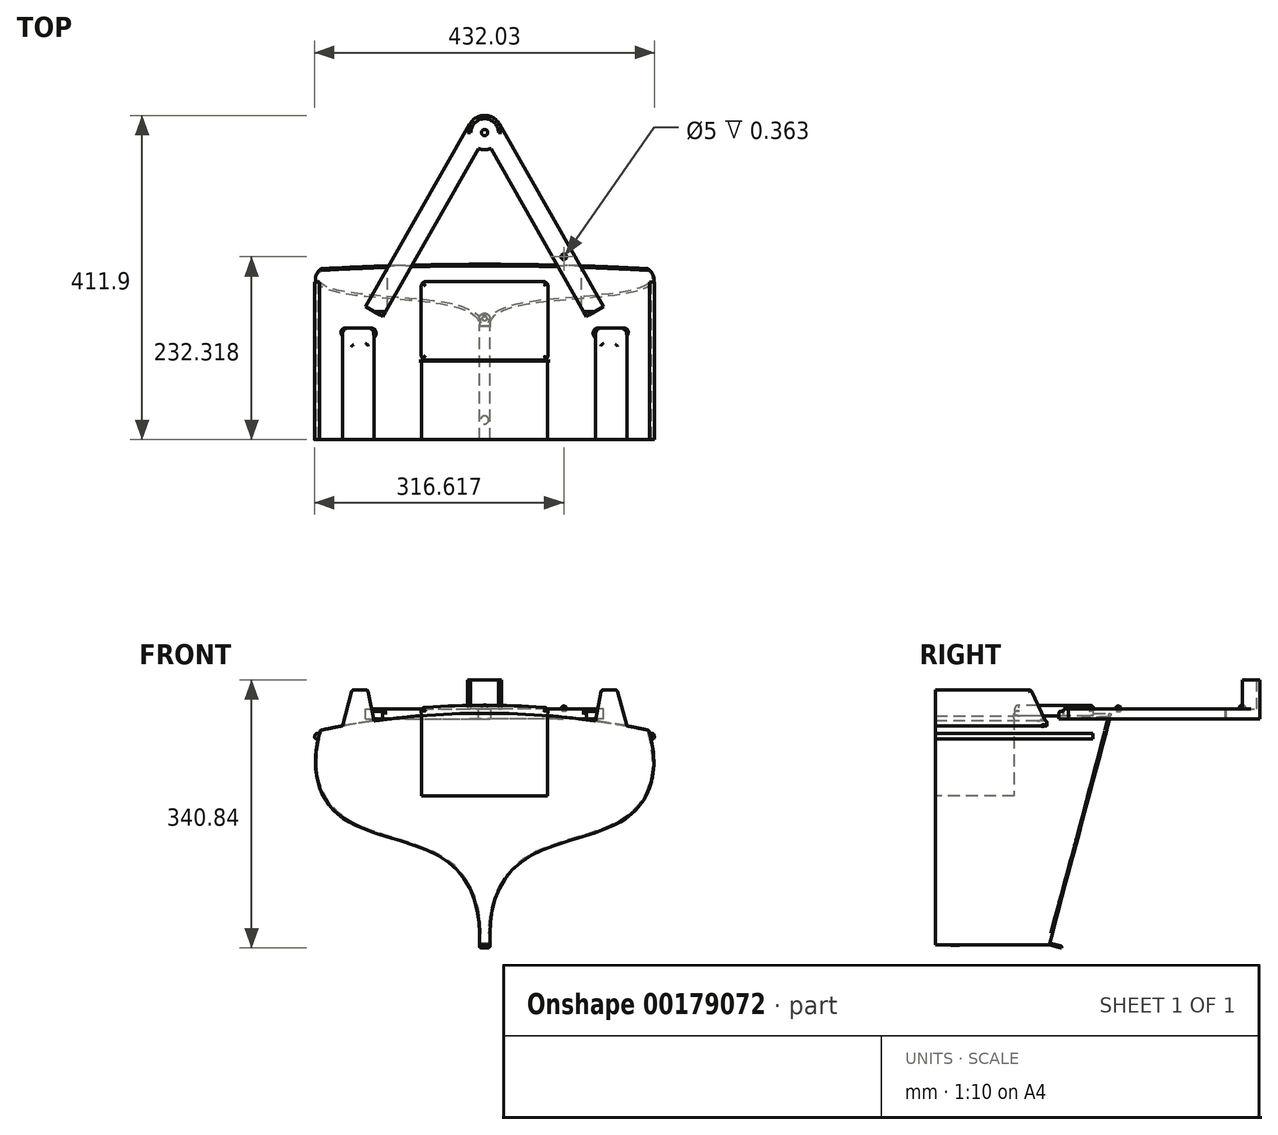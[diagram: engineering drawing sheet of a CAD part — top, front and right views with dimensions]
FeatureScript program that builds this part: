
annotation { "Feature Type Name" : "Feature", "Feature Type Description" : "" }
export const myFeature = defineFeature(function(context is Context, id is Id, definition is map)
    precondition{}
    {
        {
            var Q0;
            Q0=qCreatedBy(makeId("Front.planeOp"),FACE);
            var sketch = newSketch(context, id + "F0", { "sketchPlane" : qUnion([Q0])});
            skLineSegment(sketch, "E0", {"start": v(-1.33, 107.49) * mm, "end": v(-1.33, -186.7) * mm});
            skLineSegment(sketch, "E1", {"start": v(-1.33, -186.7) * mm, "end": v(-8, -186.7) * mm});
            skLineSegment(sketch, "E2", {"start": v(-1.33, -186.7) * mm, "end": v(-1.33, -544.52) * mm});
            skLineSegment(sketch, "E3", {"start": v(-8, -186.7) * mm, "end": v(-8, -172.3) * mm});
            skFitSpline(sketch, "E4", {"points": [v(-8, -172.3) * mm, v(-51.5, -78.76) * mm, v(-184.88, -23.02) * mm, v(-209.95, 85.87) * mm], "startDerivative": vector(0, 354.93) * mm, "endDerivative": vector(127.36, 421.05) * mm});
            skFitSpline(sketch, "E5.MirrorCS", {"points": [v(5.35, -172.3) * mm, v(48.84, -78.76) * mm, v(182.22, -23.02) * mm, v(207.3, 85.87) * mm], "startDerivative": vector(0, 354.93) * mm, "endDerivative": vector(-127.36, 421.05) * mm});
            skLineSegment(sketch, "E6.MirrorCS", {"start": v(5.35, -186.7) * mm, "end": v(5.35, -172.3) * mm});
            skLineSegment(sketch, "E7.MirrorCS", {"start": v(-1.33, -186.7) * mm, "end": v(5.35, -186.7) * mm});
            skArc(sketch, "E8", {"start": v(207.3, 85.87) * mm, "mid": v(-1.33, 107.49) * mm, "end": v(-209.95, 85.87) * mm});
            skSolve(sketch);
        }
        {
            var Q0;
            {var subQ2=sQuery(id+"F0.wireOp",EDGE,"E0");Q0=makeQuery(id+"F0.imprint","IMPRINT",FACE,{"disambiguationData":[TD([[makeQuery(id+"F0.imprint","IMPRINT",EDGE,{"derivedFrom":subQ2}),-1.0]])]});}
            var Q1;
            {var subQ1=sQuery(id+"F0.wireOp",EDGE,"E0");Q1=makeQuery(id+"F0.imprint","IMPRINT",FACE,{"disambiguationData":[TD([[makeQuery(id+"F0.imprint","IMPRINT",EDGE,{"derivedFrom":subQ1}),1.0]])]});}
            extrude(context, id + "F1", {"entities" : qUnion([Q0, Q1]), "depth" : 250 * mm});
        }
        {
            var Q0;
            Q0=qCreatedBy(makeId("Right.planeOp"),FACE);
            var sketch = newSketch(context, id + "F2", { "sketchPlane" : qUnion([Q0])});
            skLineSegment(sketch, "E9", {"start": v(-105.35, -186.7) * mm, "end": v(-3.4, 193.82) * mm});
            skLineSegment(sketch, "E10", {"start": v(-3.4, 193.82) * mm, "end": v(124.64, 193.82) * mm});
            skLineSegment(sketch, "E11", {"start": v(124.64, 193.82) * mm, "end": v(124.64, -248.32) * mm});
            skLineSegment(sketch, "E12.0", {"start": v(-250, -186.7) * mm, "end": v(0, -186.7) * mm});
            skLineSegment(sketch, "E13", {"start": v(-105.35, -186.7) * mm, "end": v(124.64, -248.32) * mm});
            skSolve(sketch);
        }
        {
            var Q0;
            Q0=makeQuery(id+"F2.imprint","IMPRINT",FACE,{"disambiguationData":[TD([[makeQuery(id+"F2.imprint","IMPRINT",EDGE,{"derivedFrom":sQuery(id+"F2.wireOp",EDGE,"E9")}),-1.0]])]});
            extrude(context, id + "F3", {"entities" : qUnion([Q0]), "operationType" : NewBodyOperationType.REMOVE, "endBound" : BoundingType.SYMMETRIC, "oppositeDirection" : true, "depth" : 500 * mm});
        }
        {
            var Q0;
            Q0=makeQuery(id+"F3.boolean.opBoolean","COPY",FACE,{"derivedFrom":makeQuery(id+"F3.opExtrude","SWEPT_FACE",FACE,{"disambiguationData":[OSD([sQuery(id+"F2.wireOp",EDGE,"E9")])]})});
            var sketch = newSketch(context, id + "F4", { "sketchPlane" : qUnion([Q0])});
            skLineSegment(sketch, "E14.bottom", {"start": v(8, -207.6) * mm, "end": v(-5.35, -207.6) * mm});
            skLineSegment(sketch, "E14.top", {"start": v(8, -205.26) * mm, "end": v(-5.35, -205.26) * mm});
            skLineSegment(sketch, "E14.left", {"start": v(8, -207.6) * mm, "end": v(8, -205.26) * mm});
            skLineSegment(sketch, "E14.right", {"start": v(-5.35, -207.6) * mm, "end": v(-5.35, -205.26) * mm});
            skSolve(sketch);
        }
        {
            var Q0;
            Q0=makeQuery(id+"F4.imprint","IMPRINT",FACE,{"disambiguationData":[TD([[makeQuery(id+"F4.imprint","IMPRINT",EDGE,{"derivedFrom":sQuery(id+"F4.wireOp",EDGE,"E14.bottom")}),-1.0]])]});
            extrude(context, id + "F5", {"entities" : qUnion([Q0]), "operationType" : NewBodyOperationType.ADD, "depth" : 16 * mm});
        }
        {
            var Q0;
            Q0=makeQuery(id+"F5.opExtrude","CAP_EDGE",EDGE,{"disambiguationData":[OSD([sQuery(id+"F4.wireOp",EDGE,"E14.right")])],"isStart":false});
            var Q1;
            Q1=makeQuery(id+"F5.opExtrude","CAP_EDGE",EDGE,{"disambiguationData":[OSD([sQuery(id+"F4.wireOp",EDGE,"E14.left")])],"isStart":false});
            fillet(context, id + "F6", {"entities" : qUnion([Q0, Q1]), "radius" : 6.6 * mm, "tangentPropagation" : true, "allowEdgeOverflow" : false});
        }
        {
            var Q0;
            Q0=makeQuery(id+"F5.opExtrude","SWEPT_FACE",FACE,{"disambiguationData":[OSD([sQuery(id+"F4.wireOp",EDGE,"E14.top")])]});
            var sketch = newSketch(context, id + "F7", { "sketchPlane" : qUnion([Q0])});
            skLineSegment(sketch, "E15", {"start": v(-1.33, -53.44) * mm, "end": v(-1.4, -44.04) * mm});
            skCircle(sketch, "E16", {"center": v(-1.4, -44.04) * mm, "radius": 3 * mm});
            skSolve(sketch);
        }
        {
            var Q0;
            Q0=makeQuery(id+"F7.imprint","IMPRINT",FACE,{"disambiguationData":[TD([[makeQuery(id+"F7.imprint","IMPRINT",EDGE,{"derivedFrom":sQuery(id+"F7.wireOp",EDGE,"E16")}),1.0]])]});
            extrude(context, id + "F8", {"entities" : qUnion([Q0]), "operationType" : NewBodyOperationType.REMOVE, "oppositeDirection" : true, "depth" : 25 * mm});
        }
        {
            var Q0;
            Q0=qCreatedBy(makeId("Top.planeOp"),FACE);
            cPlane(context, id + "F9", {"entities" : qUnion([Q0]), "cplaneType" : CPlaneType.OFFSET, "offset" : 110 * mm, "width" : 150 * mm, "height" : 150 * mm});
        }
        {
            var Q0;
            Q0=qCreatedBy(id+"F9.planeOp",FACE);
            var sketch = newSketch(context, id + "F10", { "sketchPlane" : qUnion([Q0])});
            skLineSegment(sketch, "E17.0.0", {"start": v(5.35, -104.75) * mm, "end": v(-8, -104.75) * mm});
            skLineSegment(sketch, "E17.0.1", {"start": v(-8, -104.75) * mm, "end": v(-8, -101.5) * mm});
            skFitSpline(sketch, "E17.0.2", {"points": [v(-8, -101.5) * mm, v(-8, -100.45) * mm, v(-8.3, -98.35) * mm, v(-9.41, -95.75) * mm, v(-10.8, -93.7) * mm, v(-12.1, -92.15) * mm, v(-13.69, -90.62) * mm, v(-15.53, -89.13) * mm, v(-17.67, -87.66) * mm, v(-20.1, -86.23) * mm, v(-22.84, -84.82) * mm, v(-25.92, -83.45) * mm, v(-29.28, -82.15) * mm, v(-32.93, -80.9) * mm, v(-36.88, -79.72) * mm, v(-40.43, -78.8) * mm, v(-43.42, -78.08) * mm, v(-45.74, -77.57) * mm, v(-48.1, -77.08) * mm, v(-51.32, -76.45) * mm, v(-55.43, -75.73) * mm, v(-60.5, -74.95) * mm, v(-65.68, -74.24) * mm, v(-72.72, -73.36) * mm, v(-81.71, -72.38) * mm, v(-92.72, -71.33) * mm, v(-103.87, -70.36) * mm, v(-115.1, -69.44) * mm, v(-126.32, -68.52) * mm, v(-137.49, -67.57) * mm, v(-148.54, -66.54) * mm, v(-157.59, -65.58) * mm, v(-164.69, -64.73) * mm, v(-169.92, -64.03) * mm, v(-175.06, -63.27) * mm, v(-180, -62.45) * mm, v(-184.72, -61.55) * mm, v(-188.43, -60.73) * mm, v(-191.27, -60.03) * mm, v(-193.34, -59.49) * mm, v(-195.33, -58.92) * mm, v(-197.22, -58.33) * mm, v(-199.02, -57.74) * mm, v(-201.3, -56.92) * mm, v(-203.9, -55.86) * mm, v(-206.68, -54.54) * mm, v(-209.1, -53.16) * mm, v(-211.18, -51.72) * mm, v(-212.87, -50.26) * mm, v(-214.21, -48.8) * mm, v(-215.2, -47.3) * mm, v(-215.88, -45.8) * mm, v(-216.25, -44.27) * mm, v(-216.33, -42.74) * mm, v(-216.06, -40.73) * mm, v(-215.08, -38.23) * mm, v(-213, -35.26) * mm, v(-211.05, -33.3) * mm, v(-209.95, -32.32) * mm]});
            skEllipticalArc(sketch, "E17.0.3", {});
            skFitSpline(sketch, "E17.0.4", {"points": [v(207.3, -32.32) * mm, v(208.4, -33.3) * mm, v(210.34, -35.26) * mm, v(212.42, -38.23) * mm, v(213.4, -40.73) * mm, v(213.67, -42.74) * mm, v(213.6, -44.27) * mm, v(213.23, -45.8) * mm, v(212.55, -47.3) * mm, v(211.56, -48.8) * mm, v(210.22, -50.26) * mm, v(208.53, -51.72) * mm, v(206.45, -53.16) * mm, v(204.03, -54.54) * mm, v(201.25, -55.86) * mm, v(198.64, -56.92) * mm, v(196.37, -57.74) * mm, v(194.57, -58.33) * mm, v(192.68, -58.92) * mm, v(190.68, -59.49) * mm, v(188.62, -60.03) * mm, v(185.78, -60.73) * mm, v(182.06, -61.55) * mm, v(177.35, -62.45) * mm, v(172.4, -63.27) * mm, v(167.27, -64.03) * mm, v(162.03, -64.73) * mm, v(154.93, -65.58) * mm, v(145.88, -66.54) * mm, v(134.83, -67.57) * mm, v(123.66, -68.52) * mm, v(112.44, -69.44) * mm, v(101.22, -70.36) * mm, v(90.07, -71.33) * mm, v(79.06, -72.38) * mm, v(70.07, -73.36) * mm, v(63.03, -74.24) * mm, v(57.85, -74.95) * mm, v(52.78, -75.73) * mm, v(48.67, -76.45) * mm, v(45.46, -77.08) * mm, v(43.09, -77.57) * mm, v(40.76, -78.08) * mm, v(37.77, -78.8) * mm, v(34.23, -79.72) * mm, v(30.28, -80.9) * mm, v(26.62, -82.15) * mm, v(23.27, -83.45) * mm, v(20.19, -84.82) * mm, v(17.44, -86.23) * mm, v(15.01, -87.66) * mm, v(12.88, -89.13) * mm, v(11.03, -90.62) * mm, v(9.45, -92.15) * mm, v(8.15, -93.7) * mm, v(6.76, -95.75) * mm, v(5.64, -98.35) * mm, v(5.35, -100.45) * mm, v(5.35, -101.5) * mm]});
            skLineSegment(sketch, "E17.0.5", {"start": v(5.35, -101.5) * mm, "end": v(5.35, -104.75) * mm});
            skLineSegment(sketch, "E18", {"start": v(-1.33, -26.53) * mm, "end": v(-1.33, 140.14) * mm});
            skArc(sketch, "E19", {"start": v(17.58, 150.92) * mm, "mid": v(-1.33, 161.9) * mm, "end": v(-20.24, 150.92) * mm});
            skLineSegment(sketch, "E20", {"start": v(119.81, -28.47) * mm, "end": v(17.58, 150.92) * mm});
            skLineSegment(sketch, "E21", {"start": v(119.81, -28.47) * mm, "end": v(149.75, -81) * mm});
            skLineSegment(sketch, "E22", {"start": v(149.75, -81) * mm, "end": v(128.03, -93.38) * mm});
            skLineSegment(sketch, "E23", {"start": v(128.03, -93.38) * mm, "end": v(6.52, 119.84) * mm});
            skLineSegment(sketch, "E24.MirrorCS", {"start": v(-130.68, -93.38) * mm, "end": v(-9.17, 119.84) * mm});
            skLineSegment(sketch, "E25.MirrorCS", {"start": v(-122.46, -28.47) * mm, "end": v(-20.24, 150.92) * mm});
            skLineSegment(sketch, "E26.MirrorCS", {"start": v(-122.46, -28.47) * mm, "end": v(-152.4, -81) * mm});
            skLineSegment(sketch, "E27.MirrorCS", {"start": v(-152.4, -81) * mm, "end": v(-130.68, -93.38) * mm});
            skArc(sketch, "E28.trimOffspring", {"start": v(-9.17, 119.84) * mm, "mid": v(-1.33, 118.38) * mm, "end": v(6.52, 119.84) * mm});
            const initialGuessF10  = {"E17.0.3": [-0.001326968142953605, -0.29910888352147796, 1, 0, 1.0172835059924696, 0.27258029390418276, 1.3642566717496463, 1.777335981840147]};
            skSetInitialGuess(sketch, initialGuessF10);
            skSolve(sketch);
        }
        {
            var Q0;
            Q0=makeQuery(id+"F10.imprint","IMPRINT",FACE,{"disambiguationData":[TD([[makeQuery(id+"F10.imprint","IMPRINT",EDGE,{"derivedFrom":sQuery(id+"F10.wireOp",EDGE,"E19")}),1.0]])]});
            var Q1;
            {var subQ0=sQuery(id+"F10.wireOp",EDGE,"E21");var subQ5=sQuery(id+"F10.wireOp",EDGE,"E17.0.4");var subQ6=makeQuery(id+"F10.imprint","INTERSECT",VERTEX,{"derivedFrom":[subQ5,subQ0]});Q1=makeQuery(id+"F10.imprint","IMPRINT",FACE,{"disambiguationData":[TD([[makeQuery(id+"F10.imprint","IMPRINT",EDGE,{"disambiguationData":[TD([[subQ6,-1.0]])],"derivedFrom":subQ5}),-1.0]])]});}
            var Q2;
            {var subQ5=sQuery(id+"F10.wireOp",EDGE,"E22");Q2=makeQuery(id+"F10.imprint","IMPRINT",FACE,{"disambiguationData":[TD([[makeQuery(id+"F10.imprint","IMPRINT",EDGE,{"derivedFrom":subQ5}),-1.0]])]});}
            var Q3;
            {var subQ0=sQuery(id+"F10.wireOp",EDGE,"E24.MirrorCS");var subQ1=sQuery(id+"F10.wireOp",EDGE,"E17.0.2");var subQ2=makeQuery(id+"F10.imprint","INTERSECT",VERTEX,{"derivedFrom":[subQ1,subQ0]});Q3=makeQuery(id+"F10.imprint","IMPRINT",FACE,{"disambiguationData":[TD([[makeQuery(id+"F10.imprint","IMPRINT",EDGE,{"disambiguationData":[TD([[subQ2,-1.0]])],"derivedFrom":subQ1}),-1.0]])]});}
            var Q4;
            {var subQ5=sQuery(id+"F10.wireOp",EDGE,"E27.MirrorCS");Q4=makeQuery(id+"F10.imprint","IMPRINT",FACE,{"disambiguationData":[TD([[makeQuery(id+"F10.imprint","IMPRINT",EDGE,{"derivedFrom":subQ5}),1.0]])]});}
            extrude(context, id + "F11", {"entities" : qUnion([Q0, Q1, Q2, Q3, Q4]), "operationType" : NewBodyOperationType.ADD, "oppositeDirection" : true, "depth" : 10 * mm});
        }
        {
            var Q0;
            Q0=makeQuery(id+"F11.opExtrude","CAP_FACE",FACE,{"disambiguationData":[OSD([sQuery(id+"F10.wireOp",EDGE,"E19"),sQuery(id+"F10.wireOp",EDGE,"E20"),sQuery(id+"F10.wireOp",EDGE,"E21"),sQuery(id+"F10.wireOp",EDGE,"E22"),sQuery(id+"F10.wireOp",EDGE,"E23"),sQuery(id+"F10.wireOp",EDGE,"E24.MirrorCS"),sQuery(id+"F10.wireOp",EDGE,"E25.MirrorCS"),sQuery(id+"F10.wireOp",EDGE,"E26.MirrorCS"),sQuery(id+"F10.wireOp",EDGE,"E27.MirrorCS"),sQuery(id+"F10.wireOp",EDGE,"E28.trimOffspring")])],"isStart":true});
            var sketch = newSketch(context, id + "F12", { "sketchPlane" : qUnion([Q0])});
            skArc(sketch, "E29", {"start": v(20.44, 140.14) * mm, "mid": v(-1.33, 161.9) * mm, "end": v(-23.1, 140.14) * mm});
            skArc(sketch, "E30", {"start": v(16.26, 140.14) * mm, "mid": v(-1.33, 157.73) * mm, "end": v(-18.91, 140.14) * mm});
            skLineSegment(sketch, "E31", {"start": v(-1.33, 140.14) * mm, "end": v(-23.1, 140.14) * mm});
            skLineSegment(sketch, "E32", {"start": v(16.26, 140.14) * mm, "end": v(20.44, 140.14) * mm});
            skSolve(sketch);
        }
        {
            var Q0;
            Q0=makeQuery(id+"F12.imprint","IMPRINT",FACE,{"disambiguationData":[TD([[makeQuery(id+"F12.imprint","IMPRINT",EDGE,{"derivedFrom":sQuery(id+"F12.wireOp",EDGE,"E30")}),-1.0]])]});
            extrude(context, id + "F13", {"entities" : qUnion([Q0]), "operationType" : NewBodyOperationType.ADD, "depth" : 40 * mm});
        }
        {
            var Q0;
            Q0=makeQuery(id+"F11.opExtrude","CAP_FACE",FACE,{"disambiguationData":[OSD([sQuery(id+"F10.wireOp",EDGE,"E19"),sQuery(id+"F10.wireOp",EDGE,"E20"),sQuery(id+"F10.wireOp",EDGE,"E21"),sQuery(id+"F10.wireOp",EDGE,"E22"),sQuery(id+"F10.wireOp",EDGE,"E23"),sQuery(id+"F10.wireOp",EDGE,"E24.MirrorCS"),sQuery(id+"F10.wireOp",EDGE,"E25.MirrorCS"),sQuery(id+"F10.wireOp",EDGE,"E26.MirrorCS"),sQuery(id+"F10.wireOp",EDGE,"E27.MirrorCS"),sQuery(id+"F10.wireOp",EDGE,"E28.trimOffspring")])],"isStart":true});
            var sketch = newSketch(context, id + "F14", { "sketchPlane" : qUnion([Q0])});
            skLineSegment(sketch, "E33", {"start": v(-141.54, -87.19) * mm, "end": v(-101.93, -17.68) * mm});
            skCircle(sketch, "E34", {"center": v(-101.93, -17.68) * mm, "radius": 2.5 * mm});
            skLineSegment(sketch, "E35", {"start": v(-141.54, -87.19) * mm, "end": v(138.89, -87.19) * mm});
            skLineSegment(sketch, "E36", {"start": v(-1.33, -87.19) * mm, "end": v(-1.33, 21.86) * mm});
            skCircle(sketch, "E37.MirrorC", {"center": v(99.28, -17.68) * mm, "radius": 2.5 * mm});
            skSolve(sketch);
        }
        {
            var Q0;
            Q0=makeQuery(id+"F14.imprint","IMPRINT",FACE,{"disambiguationData":[TD([[makeQuery(id+"F14.imprint","IMPRINT",EDGE,{"derivedFrom":sQuery(id+"F14.wireOp",EDGE,"E34")}),1.0]])]});
            var Q1;
            Q1=makeQuery(id+"F14.imprint","IMPRINT",FACE,{"disambiguationData":[TD([[makeQuery(id+"F14.imprint","IMPRINT",EDGE,{"derivedFrom":sQuery(id+"F14.wireOp",EDGE,"E37.MirrorC")}),-1.0]])]});
            extrude(context, id + "F15", {"entities" : qUnion([Q0, Q1]), "operationType" : NewBodyOperationType.ADD, "depth" : 3 * mm});
        }
        {
            var Q0;
            Q0=makeQuery(id+"F11.opExtrude","CAP_EDGE",EDGE,{"disambiguationData":[OSD([sQuery(id+"F10.wireOp",EDGE,"E20"),sQuery(id+"F10.wireOp",EDGE,"E21")])],"isStart":true});
            var Q1;
            Q1=makeQuery(id+"F11.opExtrude","CAP_EDGE",EDGE,{"disambiguationData":[OSD([sQuery(id+"F10.wireOp",EDGE,"E23")])],"isStart":true});
            var Q2;
            Q2=makeQuery(id+"F11.opExtrude","CAP_EDGE",EDGE,{"disambiguationData":[OSD([sQuery(id+"F10.wireOp",EDGE,"E24.MirrorCS")])],"isStart":true});
            var Q3;
            Q3=makeQuery(id+"F11.opExtrude","CAP_EDGE",EDGE,{"disambiguationData":[OSD([sQuery(id+"F10.wireOp",EDGE,"E25.MirrorCS"),sQuery(id+"F10.wireOp",EDGE,"E26.MirrorCS")])],"isStart":true});
            fillet(context, id + "F16", {"entities" : qUnion([Q0, Q1, Q2, Q3]), "radius" : 4 * mm, "tangentPropagation" : true, "allowEdgeOverflow" : false});
        }
        {
            var Q0;
            Q0=makeQuery(id+"F1.opExtrude","CAP_FACE",FACE,{"disambiguationData":[OSD([sQuery(id+"F0.wireOp",EDGE,"E1"),sQuery(id+"F0.wireOp",EDGE,"E3"),sQuery(id+"F0.wireOp",EDGE,"E4"),sQuery(id+"F0.wireOp",EDGE,"E5.MirrorCS"),sQuery(id+"F0.wireOp",EDGE,"E6.MirrorCS"),sQuery(id+"F0.wireOp",EDGE,"E7.MirrorCS"),sQuery(id+"F0.wireOp",EDGE,"E8")])],"isStart":false});
            var sketch = newSketch(context, id + "F17", { "sketchPlane" : qUnion([Q0])});
            skLineSegment(sketch, "E38.bottom", {"start": v(78.67, 128.43) * mm, "end": v(-81.33, 128.43) * mm});
            skLineSegment(sketch, "E38.top", {"start": v(78.67, 2.4) * mm, "end": v(-81.33, 2.4) * mm});
            skLineSegment(sketch, "E38.left", {"start": v(78.67, 128.43) * mm, "end": v(78.67, 2.4) * mm});
            skLineSegment(sketch, "E38.right", {"start": v(-81.33, 128.43) * mm, "end": v(-81.33, 2.4) * mm});
            skLineSegment(sketch, "E39.0", {"start": v(5.35, -186.7) * mm, "end": v(-8, -186.7) * mm});
            skLineSegment(sketch, "E40", {"start": v(-1.33, -186.7) * mm, "end": v(-1.33, -46.93) * mm});
            skSolve(sketch);
        }
        {
            var Q0;
            {var subQ0=sQuery(id+"F17.wireOp",EDGE,"E38.bottom");Q0=makeQuery(id+"F17.imprint","IMPRINT",FACE,{"disambiguationData":[TD([[makeQuery(id+"F17.imprint","IMPRINT",EDGE,{"derivedFrom":subQ0}),1.0]])]});}
            var Q1;
            {var subQ0=sQuery(id+"F17.wireOp",EDGE,"E38.top");Q1=makeQuery(id+"F17.imprint","IMPRINT",FACE,{"disambiguationData":[TD([[makeQuery(id+"F17.imprint","IMPRINT",EDGE,{"derivedFrom":subQ0}),-1.0]])]});}
            extrude(context, id + "F18", {"entities" : qUnion([Q0, Q1]), "operationType" : NewBodyOperationType.REMOVE, "oppositeDirection" : true, "depth" : 100 * mm});
        }
        {
            var Q0;
            Q0=makeQuery(id+"F15.opExtrude","CAP_FACE",FACE,{"disambiguationData":[OSD([sQuery(id+"F14.wireOp",EDGE,"E37.MirrorC")])],"isStart":false});
            var sketch = newSketch(context, id + "F19", { "sketchPlane" : qUnion([Q0])});
            skLineSegment(sketch, "E41", {"start": v(99.28, -14.05) * mm, "end": v(99.28, -21.32) * mm});
            skArc(sketch, "E42", {"start": v(99.28, -14.05) * mm, "mid": v(95.64, -17.68) * mm, "end": v(99.28, -21.32) * mm});
            skSolve(sketch);
        }
        {
            var Q0;
            {var subQ0=sQuery(id+"F19.wireOp",EDGE,"E42");Q0=makeQuery(id+"F19.imprint","IMPRINT",FACE,{"disambiguationData":[TD([[makeQuery(id+"F19.imprint","IMPRINT",EDGE,{"derivedFrom":subQ0}),1.0]])]});}
            var Q1;
            {var subQ0=sQuery(id+"F19.wireOp",EDGE,"E41");var subQ1=makeQuery(id+"F15.opExtrude","CAP_EDGE",EDGE,{"disambiguationData":[OSD([sQuery(id+"F14.wireOp",EDGE,"E37.MirrorC")])],"isStart":false});var subQ2=makeQuery(id+"F19.imprint","INTERSECT",VERTEX,{"disambiguationData":[OD(0.0)],"derivedFrom":[subQ1,subQ0]});Q1=makeQuery(id+"F19.imprint","IMPRINT",FACE,{"disambiguationData":[TD([[makeQuery(id+"F19.imprint","IMPRINT",EDGE,{"disambiguationData":[TD([[subQ2,-1.0]])],"derivedFrom":subQ0}),-1.0]])]});}
            var Q2;
            Q2=sQuery(id+"F19.wireOp",EDGE,"E41");
            revolve(context, id + "F20", {"operationType" : NewBodyOperationType.ADD, "entities" : qUnion([Q0, Q1]), "axis" : qUnion([Q2]), "revolveType" : RevolveType.FULL});
        }
        {
            var Q0;
            Q0=makeQuery(id+"F11.opExtrude","CAP_FACE",FACE,{"disambiguationData":[OSD([sQuery(id+"F10.wireOp",EDGE,"E19"),sQuery(id+"F10.wireOp",EDGE,"E20"),sQuery(id+"F10.wireOp",EDGE,"E21"),sQuery(id+"F10.wireOp",EDGE,"E22"),sQuery(id+"F10.wireOp",EDGE,"E23"),sQuery(id+"F10.wireOp",EDGE,"E24.MirrorCS"),sQuery(id+"F10.wireOp",EDGE,"E25.MirrorCS"),sQuery(id+"F10.wireOp",EDGE,"E26.MirrorCS"),sQuery(id+"F10.wireOp",EDGE,"E27.MirrorCS"),sQuery(id+"F10.wireOp",EDGE,"E28.trimOffspring")])],"isStart":true});
            var sketch = newSketch(context, id + "F21", { "sketchPlane" : qUnion([Q0])});
            skCircle(sketch, "E43", {"center": v(-1.33, 140.14) * mm, "radius": 2.31 * mm});
            skSolve(sketch);
        }
        {
            var Q0;
            Q0=makeQuery(id+"F21.imprint","IMPRINT",FACE,{"disambiguationData":[TD([[makeQuery(id+"F21.imprint","IMPRINT",EDGE,{"derivedFrom":sQuery(id+"F21.wireOp",EDGE,"E43")}),1.0]])]});
            extrude(context, id + "F22", {"entities" : qUnion([Q0]), "operationType" : NewBodyOperationType.ADD, "depth" : 4 * mm});
        }
        {
            var Q0;
            Q0=makeQuery(id+"F22.opExtrude","CAP_FACE",FACE,{"disambiguationData":[OSD([sQuery(id+"F21.wireOp",EDGE,"E43")])],"isStart":false});
            var sketch = newSketch(context, id + "F23", { "sketchPlane" : qUnion([Q0])});
            skLineSegment(sketch, "E44", {"start": v(-1.33, 144.16) * mm, "end": v(-1.33, 136.12) * mm});
            skArc(sketch, "E45", {"start": v(-1.33, 144.16) * mm, "mid": v(-5.34, 140.14) * mm, "end": v(-1.33, 136.12) * mm});
            skSolve(sketch);
        }
        {
            var Q0;
            {var subQ0=sQuery(id+"F23.wireOp",EDGE,"E45");Q0=makeQuery(id+"F23.imprint","IMPRINT",FACE,{"disambiguationData":[TD([[makeQuery(id+"F23.imprint","IMPRINT",EDGE,{"derivedFrom":subQ0}),1.0]])]});}
            var Q1;
            {var subQ0=sQuery(id+"F23.wireOp",EDGE,"E44");var subQ1=makeQuery(id+"F22.opExtrude","CAP_EDGE",EDGE,{"disambiguationData":[OSD([sQuery(id+"F21.wireOp",EDGE,"E43")])],"isStart":false});var subQ2=makeQuery(id+"F23.imprint","INTERSECT",VERTEX,{"disambiguationData":[OD(0.0)],"derivedFrom":[subQ1,subQ0]});Q1=makeQuery(id+"F23.imprint","IMPRINT",FACE,{"disambiguationData":[TD([[makeQuery(id+"F23.imprint","IMPRINT",EDGE,{"disambiguationData":[TD([[subQ2,-1.0]])],"derivedFrom":subQ0}),-1.0]])]});}
            var Q2;
            Q2=sQuery(id+"F23.wireOp",EDGE,"E44");
            revolve(context, id + "F24", {"operationType" : NewBodyOperationType.ADD, "entities" : qUnion([Q0, Q1]), "axis" : qUnion([Q2]), "revolveType" : RevolveType.FULL});
        }
        {
            var Q0;
            Q0=makeQuery(id+"F1.opExtrude","CAP_FACE",FACE,{"disambiguationData":[OSD([sQuery(id+"F0.wireOp",EDGE,"E1"),sQuery(id+"F0.wireOp",EDGE,"E3"),sQuery(id+"F0.wireOp",EDGE,"E4"),sQuery(id+"F0.wireOp",EDGE,"E5.MirrorCS"),sQuery(id+"F0.wireOp",EDGE,"E6.MirrorCS"),sQuery(id+"F0.wireOp",EDGE,"E7.MirrorCS"),sQuery(id+"F0.wireOp",EDGE,"E8")])],"isStart":false});
            var sketch = newSketch(context, id + "F25", { "sketchPlane" : qUnion([Q0])});
            skLineSegment(sketch, "E46.0", {"start": v(78.67, 2.4) * mm, "end": v(-81.33, 2.4) * mm});
            skArc(sketch, "E47.0", {"start": v(207.3, 85.87) * mm, "mid": v(143.28, 97.16) * mm, "end": v(78.67, 104.34) * mm});
            skLineSegment(sketch, "E48", {"start": v(179.3, 91.32) * mm, "end": v(166.96, 137.34) * mm});
            skPoint(sketch, "E48.endSnap0", {"position": v(143.28, 97.16) * mm});
            skLineSegment(sketch, "E49", {"start": v(139.3, 97.72) * mm, "end": v(146.96, 137.34) * mm});
            skLineSegment(sketch, "E50", {"start": v(166.96, 137.34) * mm, "end": v(146.96, 137.34) * mm});
            skPoint(sketch, "E51.trimOffspring.end.orphan", {"position": v(143.28, 225.73) * mm});
            skLineSegment(sketch, "E52", {"start": v(-1.33, 2.4) * mm, "end": v(-1.33, -47.09) * mm});
            skLineSegment(sketch, "E53.MirrorCS", {"start": v(-141.95, 97.72) * mm, "end": v(-149.62, 137.34) * mm});
            skLineSegment(sketch, "E54.MirrorCS", {"start": v(-181.95, 91.32) * mm, "end": v(-169.62, 137.34) * mm});
            skLineSegment(sketch, "E55.MirrorCS", {"start": v(-169.62, 137.34) * mm, "end": v(-149.62, 137.34) * mm});
            skSolve(sketch);
        }
        {
            var Q0;
            {var subQ0=sQuery(id+"F25.wireOp",EDGE,"E48");Q0=makeQuery(id+"F25.imprint","IMPRINT",FACE,{"disambiguationData":[TD([[makeQuery(id+"F25.imprint","IMPRINT",EDGE,{"derivedFrom":subQ0}),1.0]])]});}
            var Q1;
            {var subQ0=sQuery(id+"F25.wireOp",EDGE,"E53.MirrorCS");Q1=makeQuery(id+"F25.imprint","IMPRINT",FACE,{"disambiguationData":[TD([[makeQuery(id+"F25.imprint","IMPRINT",EDGE,{"derivedFrom":subQ0}),1.0]])]});}
            extrude(context, id + "F26", {"entities" : qUnion([Q0, Q1]), "operationType" : NewBodyOperationType.ADD, "oppositeDirection" : true, "depth" : 140 * mm});
        }
        {
            var Q0;
            Q0=makeQuery(id+"F18.boolean.opBoolean","COPY",FACE,{"derivedFrom":makeQuery(id+"F18.opExtrude","CAP_FACE",FACE,{"disambiguationData":[OSD([sQuery(id+"F17.wireOp",EDGE,"E38.bottom"),sQuery(id+"F17.wireOp",EDGE,"E38.top"),sQuery(id+"F17.wireOp",EDGE,"E38.left"),sQuery(id+"F17.wireOp",EDGE,"E38.right")])],"isStart":false})});
            cPlane(context, id + "F27", {"entities" : qUnion([Q0]), "cplaneType" : CPlaneType.OFFSET, "offset" : 1 * mm, "oppositeDirection" : true, "width" : 150 * mm, "height" : 150 * mm});
        }
        {
            var Q0;
            Q0=qCreatedBy(id+"F27.planeOp",FACE);
            var sketch = newSketch(context, id + "F28", { "sketchPlane" : qUnion([Q0])});
            skArc(sketch, "E56.0", {"start": v(78.67, 104.34) * mm, "mid": v(-1.33, 107.49) * mm, "end": v(-81.33, 104.34) * mm});
            skArc(sketch, "E57.0", {"start": v(79.46, 114.3) * mm, "mid": v(-1.33, 117.49) * mm, "end": v(-82.11, 114.3) * mm});
            skLineSegment(sketch, "E58", {"start": v(-81.33, 104.34) * mm, "end": v(-82.11, 114.3) * mm});
            skLineSegment(sketch, "E59", {"start": v(78.67, 104.34) * mm, "end": v(79.46, 114.3) * mm});
            skSolve(sketch);
        }
        {
            var Q0;
            Q0=makeQuery(id+"F28.imprint","IMPRINT",FACE,{"disambiguationData":[TD([[makeQuery(id+"F28.imprint","IMPRINT",EDGE,{"derivedFrom":sQuery(id+"F28.wireOp",EDGE,"E56.0")}),-1.0]])]});
            extrude(context, id + "F29", {"entities" : qUnion([Q0]), "operationType" : NewBodyOperationType.ADD, "oppositeDirection" : true, "depth" : 100 * mm});
        }
        {
            var Q0;
            Q0=makeQuery(id+"F29.opExtrude","CAP_EDGE",EDGE,{"disambiguationData":[OSD([sQuery(id+"F28.wireOp",EDGE,"E59")])],"isStart":true});
            var Q1;
            Q1=makeQuery(id+"F29.opExtrude","CAP_EDGE",EDGE,{"disambiguationData":[OSD([sQuery(id+"F28.wireOp",EDGE,"E58")])],"isStart":true});
            var Q2;
            Q2=makeQuery(id+"F29.opExtrude","CAP_EDGE",EDGE,{"disambiguationData":[OSD([sQuery(id+"F28.wireOp",EDGE,"E59")])],"isStart":false});
            var Q3;
            Q3=makeQuery(id+"F29.opExtrude","CAP_EDGE",EDGE,{"disambiguationData":[OSD([sQuery(id+"F28.wireOp",EDGE,"E58")])],"isStart":false});
            fillet(context, id + "F30", {"entities" : qUnion([Q0, Q1, Q2, Q3]), "radius" : 6 * mm, "tangentPropagation" : true, "allowEdgeOverflow" : false});
        }
        {
            var Q0;
            Q0=makeQuery(id+"F29.opExtrude","CAP_EDGE",EDGE,{"disambiguationData":[OSD([sQuery(id+"F28.wireOp",EDGE,"E57.0")])],"isStart":false});
            fillet(context, id + "F31", {"entities" : qUnion([Q0]), "radius" : 4 * mm, "tangentPropagation" : true, "allowEdgeOverflow" : false});
        }
        {
            var Q0;
            Q0=makeQuery(id+"F3.boolean.opBoolean","INTERSECT",EDGE,{"derivedFrom":[makeQuery(id+"F1.opExtrude","SWEPT_FACE",FACE,{"disambiguationData":[OSD([sQuery(id+"F0.wireOp",EDGE,"E5.MirrorCS")])]}),makeQuery(id+"F3.opExtrude","SWEPT_FACE",FACE,{"disambiguationData":[OSD([sQuery(id+"F2.wireOp",EDGE,"E9")])]})]});
            var Q1;
            Q1=makeQuery(id+"F3.boolean.opBoolean","INTERSECT",EDGE,{"derivedFrom":[makeQuery(id+"F1.opExtrude","SWEPT_FACE",FACE,{"disambiguationData":[OSD([sQuery(id+"F0.wireOp",EDGE,"E4")])]}),makeQuery(id+"F3.opExtrude","SWEPT_FACE",FACE,{"disambiguationData":[OSD([sQuery(id+"F2.wireOp",EDGE,"E9")])]})]});
            var Q2;
            Q2=makeQuery(id+"F1.opExtrude","SWEPT_EDGE",EDGE,{"disambiguationData":[OSD([sQuery(id+"F0.wireOp",EDGE,"E5.MirrorCS"),sQuery(id+"F0.wireOp",EDGE,"E8")])]});
            var Q3;
            {var subQ0=makeQuery(id+"F1.opExtrude","SWEPT_FACE",FACE,{"disambiguationData":[OSD([sQuery(id+"F0.wireOp",EDGE,"E8")])]});var subQ1=makeQuery(id+"F3.opExtrude","SWEPT_FACE",FACE,{"disambiguationData":[OSD([sQuery(id+"F2.wireOp",EDGE,"E9")])]});Q3=makeQuery(id+"F11.boolean.opBoolean","SPLIT",EDGE,{"disambiguationData":[TD([makeQuery(id+"F1.opExtrude","SWEPT_FACE",FACE,{"disambiguationData":[OSD([sQuery(id+"F0.wireOp",EDGE,"E5.MirrorCS")])]})])],"derivedFrom":makeQuery(id+"F3.boolean.opBoolean","INTERSECT",EDGE,{"derivedFrom":[subQ0,subQ1]})});}
            var Q4;
            {var subQ0=makeQuery(id+"F1.opExtrude","SWEPT_FACE",FACE,{"disambiguationData":[OSD([sQuery(id+"F0.wireOp",EDGE,"E8")])]});var subQ1=makeQuery(id+"F3.opExtrude","SWEPT_FACE",FACE,{"disambiguationData":[OSD([sQuery(id+"F2.wireOp",EDGE,"E9")])]});Q4=makeQuery(id+"F11.boolean.opBoolean","SPLIT",EDGE,{"disambiguationData":[TD([makeQuery(id+"F11.opExtrude","SWEPT_FACE",FACE,{"disambiguationData":[OSD([sQuery(id+"F10.wireOp",EDGE,"E23")])]})])],"derivedFrom":makeQuery(id+"F3.boolean.opBoolean","INTERSECT",EDGE,{"derivedFrom":[subQ0,subQ1]})});}
            var Q5;
            {var subQ0=makeQuery(id+"F1.opExtrude","SWEPT_FACE",FACE,{"disambiguationData":[OSD([sQuery(id+"F0.wireOp",EDGE,"E8")])]});var subQ1=makeQuery(id+"F3.opExtrude","SWEPT_FACE",FACE,{"disambiguationData":[OSD([sQuery(id+"F2.wireOp",EDGE,"E9")])]});Q5=makeQuery(id+"F11.boolean.opBoolean","SPLIT",EDGE,{"disambiguationData":[TD([makeQuery(id+"F1.opExtrude","SWEPT_FACE",FACE,{"disambiguationData":[OSD([sQuery(id+"F0.wireOp",EDGE,"E4")])]})])],"derivedFrom":makeQuery(id+"F3.boolean.opBoolean","INTERSECT",EDGE,{"derivedFrom":[subQ0,subQ1]})});}
            var Q6;
            Q6=makeQuery(id+"F1.opExtrude","SWEPT_EDGE",EDGE,{"disambiguationData":[OSD([sQuery(id+"F0.wireOp",EDGE,"E4"),sQuery(id+"F0.wireOp",EDGE,"E8")])]});
            fillet(context, id + "F32", {"entities" : qUnion([Q0, Q1, Q2, Q3, Q4, Q5, Q6]), "radius" : 2 * mm, "tangentPropagation" : true, "allowEdgeOverflow" : false});
        }
        {
            var Q0;
            Q0=makeQuery(id+"F26.opExtrude","SWEPT_FACE",FACE,{"disambiguationData":[OSD([sQuery(id+"F25.wireOp",EDGE,"E50")])]});
            var sketch = newSketch(context, id + "F33", { "sketchPlane" : qUnion([Q0])});
            skLineSegment(sketch, "E60.0.0", {"start": v(-169.62, -250) * mm, "end": v(-149.62, -250) * mm});
            skLineSegment(sketch, "E60.0.1", {"start": v(-149.62, -250) * mm, "end": v(-149.62, -110) * mm});
            skLineSegment(sketch, "E60.0.2", {"start": v(-149.62, -110) * mm, "end": v(-169.62, -110) * mm});
            skLineSegment(sketch, "E60.0.3", {"start": v(-169.62, -110) * mm, "end": v(-169.62, -250) * mm});
            skLineSegment(sketch, "E61", {"start": v(166.96, -130.23) * mm, "end": v(-169.62, -130.23) * mm});
            skSolve(sketch);
        }
        {
            var Q0;
            Q0=makeQuery(id+"F26.opExtrude","CAP_VERTEX",VERTEX,{"disambiguationData":[OSD([sQuery(id+"F25.wireOp",EDGE,"E47.0"),sQuery(id+"F25.wireOp",EDGE,"E48")])],"isStart":false});
            var Q1;
            Q1=makeQuery(id+"F26.opExtrude","CAP_VERTEX",VERTEX,{"disambiguationData":[OSD([sQuery(id+"F25.wireOp",EDGE,"E47.0"),sQuery(id+"F25.wireOp",EDGE,"E49")])],"isStart":false});
            var Q2;
            Q2=sQuery(id+"F33.wireOp",VERTEX,"E61.start");
            cPlane(context, id + "F34", {"entities" : qUnion([Q0, Q1, Q2]), "cplaneType" : CPlaneType.THREE_POINT, "offset" : 25 * mm, "width" : 150 * mm, "height" : 150 * mm});
        }
        {
            var Q0;
            Q0=qCreatedBy(id+"F34.planeOp",FACE);
            var sketch = newSketch(context, id + "F35", { "sketchPlane" : qUnion([Q0])});
            skPoint(sketch, "E62.middle", {"position": v(152.55, 156.09) * mm});
            skEllipticalArc(sketch, "E63.0", {});
            skLineSegment(sketch, "E64.0", {"start": v(183.01, 128.9) * mm, "end": v(169.43, 170.72) * mm});
            skLineSegment(sketch, "E65", {"start": v(183.01, 128.9) * mm, "end": v(183.01, 203.35) * mm});
            skLineSegment(sketch, "E66", {"start": v(183.01, 203.35) * mm, "end": v(131.62, 203.35) * mm});
            skLineSegment(sketch, "E67", {"start": v(131.62, 203.35) * mm, "end": v(142.92, 134.72) * mm});
            const initialGuessF35  = {"E63.0": [0.03063310107940534, -0.7808168936861629, 0.9896498205910719, -0.14350342366668228, 1.0172835059924694, 0.9223553823554095, 1.5508849717281252, 1.5907076818616734]};
            skSetInitialGuess(sketch, initialGuessF35);
            skSolve(sketch);
        }
        {
            var Q0;
            Q0=makeQuery(id+"F35.imprint","IMPRINT",FACE,{"disambiguationData":[TD([[makeQuery(id+"F35.imprint","IMPRINT",EDGE,{"derivedFrom":sQuery(id+"F35.wireOp",EDGE,"E63.0")}),-1.0]])]});
            extrude(context, id + "F36", {"entities" : qUnion([Q0]), "operationType" : NewBodyOperationType.REMOVE, "oppositeDirection" : true, "depth" : 25 * mm});
        }
        {
            var Q0;
            Q0=makeQuery(id+"F26.opExtrude","CAP_VERTEX",VERTEX,{"disambiguationData":[OSD([sQuery(id+"F0.wireOp",EDGE,"E8"),sQuery(id+"F25.wireOp",EDGE,"E54.MirrorCS")])],"isStart":false});
            var Q1;
            Q1=makeQuery(id+"F26.opExtrude","CAP_VERTEX",VERTEX,{"disambiguationData":[OSD([sQuery(id+"F0.wireOp",EDGE,"E8"),sQuery(id+"F25.wireOp",EDGE,"E53.MirrorCS")])],"isStart":false});
            var Q2;
            Q2=sQuery(id+"F33.wireOp",VERTEX,"E61.end");
            cPlane(context, id + "F37", {"entities" : qUnion([Q0, Q1, Q2]), "cplaneType" : CPlaneType.THREE_POINT, "offset" : 25 * mm, "width" : 150 * mm, "height" : 150 * mm});
        }
        {
            var Q0;
            Q0=qCreatedBy(id+"F37.planeOp",FACE);
            var sketch = newSketch(context, id + "F38", { "sketchPlane" : qUnion([Q0])});
            skEllipticalArc(sketch, "E68.0", {});
            skLineSegment(sketch, "E69", {"start": v(145.57, 134.72) * mm, "end": v(130.43, 202.76) * mm});
            skLineSegment(sketch, "E70", {"start": v(130.43, 202.76) * mm, "end": v(202.46, 202.76) * mm});
            skLineSegment(sketch, "E71", {"start": v(202.46, 202.76) * mm, "end": v(185.66, 128.9) * mm});
            const initialGuessF38  = {"E68.0": [0.03328114275032412, -0.7808168936861628, 0.9896498205910726, -0.14350342366667695, 1.0172835059924694, 0.9223553823554093, 1.5508849717281192, 1.5907076818616674]};
            skSetInitialGuess(sketch, initialGuessF38);
            skSolve(sketch);
        }
        {
            var Q0;
            Q0=makeQuery(id+"F38.imprint","IMPRINT",FACE,{"disambiguationData":[TD([[makeQuery(id+"F38.imprint","IMPRINT",EDGE,{"derivedFrom":sQuery(id+"F38.wireOp",EDGE,"E68.0")}),-1.0]])]});
            extrude(context, id + "F39", {"entities" : qUnion([Q0]), "operationType" : NewBodyOperationType.REMOVE, "depth" : 25 * mm});
        }
        {
            var Q0;
            Q0=makeQuery(id+"F39.boolean.opBoolean","COPY",FACE,{"derivedFrom":makeQuery(id+"F39.opExtrude","CAP_FACE",FACE,{"disambiguationData":[OSD([sQuery(id+"F38.wireOp",EDGE,"E68.0"),sQuery(id+"F38.wireOp",EDGE,"E69"),sQuery(id+"F38.wireOp",EDGE,"E70"),sQuery(id+"F38.wireOp",EDGE,"E71")])],"isStart":true})});
            var Q1;
            Q1=makeQuery(id+"F36.boolean.opBoolean","COPY",FACE,{"derivedFrom":makeQuery(id+"F36.opExtrude","CAP_FACE",FACE,{"disambiguationData":[OSD([sQuery(id+"F35.wireOp",EDGE,"E63.0"),sQuery(id+"F35.wireOp",EDGE,"E65"),sQuery(id+"F35.wireOp",EDGE,"E66"),sQuery(id+"F35.wireOp",EDGE,"E67")])],"isStart":true})});
            fillet(context, id + "F40", {"entities" : qUnion([Q0, Q1]), "radius" : 3 * mm, "tangentPropagation" : true, "allowEdgeOverflow" : false});
        }
        {
            var Q0;
            Q0=makeQuery(id+"F18.boolean.opBoolean","INTERSECT",EDGE,{"derivedFrom":[makeQuery(id+"F1.opExtrude","SWEPT_FACE",FACE,{"disambiguationData":[OSD([sQuery(id+"F0.wireOp",EDGE,"E8")])]}),makeQuery(id+"F18.opExtrude","SWEPT_FACE",FACE,{"disambiguationData":[OSD([sQuery(id+"F17.wireOp",EDGE,"E38.right")])]})]});
            var Q1;
            Q1=makeQuery(id+"F18.boolean.opBoolean","INTERSECT",EDGE,{"derivedFrom":[makeQuery(id+"F1.opExtrude","SWEPT_FACE",FACE,{"disambiguationData":[OSD([sQuery(id+"F0.wireOp",EDGE,"E8")])]}),makeQuery(id+"F18.opExtrude","SWEPT_FACE",FACE,{"disambiguationData":[OSD([sQuery(id+"F17.wireOp",EDGE,"E38.left")])]})]});
            fillet(context, id + "F41", {"entities" : qUnion([Q0, Q1]), "radius" : 3 * mm, "tangentPropagation" : true, "allowEdgeOverflow" : false});
        }
        {
            var Q0;
            Q0=makeQuery(id+"F1.opExtrude","SWEPT_FACE",FACE,{"disambiguationData":[OSD([sQuery(id+"F0.wireOp",EDGE,"E1"),sQuery(id+"F0.wireOp",EDGE,"E7.MirrorCS")])]});
            var sketch = newSketch(context, id + "F42", { "sketchPlane" : qUnion([Q0])});
            skLineSegment(sketch, "E72", {"start": v(-1.33, 250) * mm, "end": v(-1.33, 224.9) * mm});
            skCircle(sketch, "E73", {"center": v(-1.33, 224.9) * mm, "radius": 5.12 * mm});
            skSolve(sketch);
        }
        {
            var Q0;
            Q0=makeQuery(id+"F42.imprint","IMPRINT",FACE,{"disambiguationData":[TD([[makeQuery(id+"F42.imprint","IMPRINT",EDGE,{"derivedFrom":sQuery(id+"F42.wireOp",EDGE,"E73")}),1.0]])]});
            extrude(context, id + "F43", {"entities" : qUnion([Q0]), "operationType" : NewBodyOperationType.ADD, "depth" : 1 * mm});
        }
        {
            var Q0;
            Q0=makeQuery(id+"F26.opExtrude","SWEPT_EDGE",EDGE,{"disambiguationData":[OSD([sQuery(id+"F25.wireOp",EDGE,"E48"),sQuery(id+"F25.wireOp",EDGE,"E50")])]});
            var Q1;
            Q1=makeQuery(id+"F26.opExtrude","SWEPT_EDGE",EDGE,{"disambiguationData":[OSD([sQuery(id+"F25.wireOp",EDGE,"E49"),sQuery(id+"F25.wireOp",EDGE,"E50")])]});
            var Q2;
            Q2=makeQuery(id+"F26.opExtrude","SWEPT_EDGE",EDGE,{"disambiguationData":[OSD([sQuery(id+"F25.wireOp",EDGE,"E53.MirrorCS"),sQuery(id+"F25.wireOp",EDGE,"E55.MirrorCS")])]});
            var Q3;
            Q3=makeQuery(id+"F26.opExtrude","SWEPT_EDGE",EDGE,{"disambiguationData":[OSD([sQuery(id+"F25.wireOp",EDGE,"E54.MirrorCS"),sQuery(id+"F25.wireOp",EDGE,"E55.MirrorCS")])]});
            var Q4;
            Q4=makeQuery(id+"F26.opExtrude","SWEPT_EDGE",EDGE,{"disambiguationData":[OSD([sQuery(id+"F25.wireOp",EDGE,"E47.0"),sQuery(id+"F25.wireOp",EDGE,"E48")])]});
            var Q5;
            Q5=makeQuery(id+"F26.opExtrude","SWEPT_EDGE",EDGE,{"disambiguationData":[OSD([sQuery(id+"F0.wireOp",EDGE,"E8"),sQuery(id+"F25.wireOp",EDGE,"E53.MirrorCS")])]});
            var Q6;
            Q6=makeQuery(id+"F26.opExtrude","SWEPT_EDGE",EDGE,{"disambiguationData":[OSD([sQuery(id+"F0.wireOp",EDGE,"E8"),sQuery(id+"F25.wireOp",EDGE,"E54.MirrorCS")])]});
            var Q7;
            Q7=makeQuery(id+"F26.opExtrude","SWEPT_EDGE",EDGE,{"disambiguationData":[OSD([sQuery(id+"F25.wireOp",EDGE,"E47.0"),sQuery(id+"F25.wireOp",EDGE,"E49")])]});
            fillet(context, id + "F44", {"entities" : qUnion([Q0, Q1, Q2, Q3, Q4, Q5, Q6, Q7]), "radius" : 3 * mm, "tangentPropagation" : true, "allowEdgeOverflow" : false});
        }
        {
            var Q0;
            {var subQ0=sQuery(id+"F0.wireOp",EDGE,"E8");Q0=makeQuery(id+"F26.boolean.opBoolean","MERGE",FACE,{"derivedFrom":[makeQuery(id+"F1.opExtrude","CAP_FACE",FACE,{"disambiguationData":[OSD([sQuery(id+"F0.wireOp",EDGE,"E1"),sQuery(id+"F0.wireOp",EDGE,"E3"),sQuery(id+"F0.wireOp",EDGE,"E4"),sQuery(id+"F0.wireOp",EDGE,"E5.MirrorCS"),sQuery(id+"F0.wireOp",EDGE,"E6.MirrorCS"),sQuery(id+"F0.wireOp",EDGE,"E7.MirrorCS"),subQ0])],"isStart":false}),makeQuery(id+"F26.opExtrude","CAP_FACE",FACE,{"disambiguationData":[OSD([sQuery(id+"F25.wireOp",EDGE,"E47.0"),sQuery(id+"F25.wireOp",EDGE,"E48"),sQuery(id+"F25.wireOp",EDGE,"E49"),sQuery(id+"F25.wireOp",EDGE,"E50")])],"isStart":true}),makeQuery(id+"F26.opExtrude","CAP_FACE",FACE,{"disambiguationData":[OSD([subQ0,sQuery(id+"F25.wireOp",EDGE,"E53.MirrorCS"),sQuery(id+"F25.wireOp",EDGE,"E54.MirrorCS"),sQuery(id+"F25.wireOp",EDGE,"E55.MirrorCS")])],"isStart":true})]});}
            var sketch = newSketch(context, id + "F45", { "sketchPlane" : qUnion([Q0])});
            skLineSegment(sketch, "E74.0", {"start": v(78.67, 2.4) * mm, "end": v(-81.33, 2.4) * mm});
            skFitSpline(sketch, "E75.0", {"points": [v(-8, -172.3) * mm, v(-8, -135.62) * mm, v(-35.41, -57.49) * mm, v(-205.36, -45.64) * mm, v(-223.65, 40.57) * mm, v(-209.95, 85.87) * mm]});
            skLineSegment(sketch, "E76", {"start": v(-1.33, 2.4) * mm, "end": v(-1.33, 115.34) * mm});
            skLineSegment(sketch, "E77", {"start": v(-212.9, 74.66) * mm, "end": v(-217.82, 75.53) * mm});
            skLineSegment(sketch, "E78", {"start": v(-211.08, 81.94) * mm, "end": v(-216.3, 81.45) * mm});
            skLineSegment(sketch, "E79", {"start": v(-216.3, 81.45) * mm, "end": v(-217.82, 75.53) * mm});
            skLineSegment(sketch, "E80.MirrorCS", {"start": v(210.25, 74.66) * mm, "end": v(215.16, 75.53) * mm});
            skLineSegment(sketch, "E81.MirrorCS", {"start": v(213.64, 81.45) * mm, "end": v(215.16, 75.53) * mm});
            skLineSegment(sketch, "E82.MirrorCS", {"start": v(208.43, 81.94) * mm, "end": v(213.64, 81.45) * mm});
            skSolve(sketch);
        }
        {
            var Q0;
            {var subQ0=sQuery(id+"F45.wireOp",EDGE,"E77");Q0=makeQuery(id+"F45.imprint","IMPRINT",FACE,{"disambiguationData":[TD([[makeQuery(id+"F45.imprint","IMPRINT",EDGE,{"derivedFrom":subQ0}),-1.0]])]});}
            var Q1;
            {var subQ0=sQuery(id+"F45.wireOp",EDGE,"E80.MirrorCS");Q1=makeQuery(id+"F45.imprint","IMPRINT",FACE,{"disambiguationData":[TD([[makeQuery(id+"F45.imprint","IMPRINT",EDGE,{"derivedFrom":subQ0}),1.0]])]});}
            extrude(context, id + "F46", {"entities" : qUnion([Q0, Q1]), "operationType" : NewBodyOperationType.ADD, "oppositeDirection" : true, "depth" : 200 * mm});
        }
        {
            var Q0;
            Q0=makeQuery(id+"F46.opExtrude","SWEPT_EDGE",EDGE,{"disambiguationData":[OSD([sQuery(id+"F45.wireOp",EDGE,"E78"),sQuery(id+"F45.wireOp",EDGE,"E79")])]});
            var Q1;
            Q1=makeQuery(id+"F46.opExtrude","SWEPT_EDGE",EDGE,{"disambiguationData":[OSD([sQuery(id+"F45.wireOp",EDGE,"E77"),sQuery(id+"F45.wireOp",EDGE,"E79")])]});
            var Q2;
            Q2=makeQuery(id+"F46.opExtrude","SWEPT_EDGE",EDGE,{"disambiguationData":[OSD([sQuery(id+"F45.wireOp",EDGE,"E81.MirrorCS"),sQuery(id+"F45.wireOp",EDGE,"E82.MirrorCS")])]});
            var Q3;
            Q3=makeQuery(id+"F46.opExtrude","SWEPT_EDGE",EDGE,{"disambiguationData":[OSD([sQuery(id+"F45.wireOp",EDGE,"E80.MirrorCS"),sQuery(id+"F45.wireOp",EDGE,"E81.MirrorCS")])]});
            fillet(context, id + "F47", {"entities" : qUnion([Q0, Q1, Q2, Q3]), "radius" : 2 * mm, "tangentPropagation" : true, "allowEdgeOverflow" : false});
        }
    });
